# Revit family: equip-bottle-filler-elkay-LK4405FRK
name_source: partatom
category: Plumbing Fixtures
units: mm (PartAtom-declared; Revit-internal decimal feet)

## family parameters
Always vertical = Yes
Cut with Voids When Loaded = No
OmniClass Number = 23.45.00.00
OmniClass Title = Sanitary, Laundry, and Cleaning Equipment
Part Type = Normal
Room Calculation Point = No
Round Connector Dimension = Use Radius
Shared = No
Work Plane-Based = No

## types (1)
- LK4405FRK
    Activation = Push Button
    Apparent Load Phase 1 = 0 VA
    Body Material = Metal - Steel - Stainless - Chrome
    Bubbler = Vandal Resistant
    CW Connection = Yes
    Chiller Option = No
    Description = Bottle Filler
    Filter = Non-filtered
    Fountain = LK4405
    HW Connection = No
    Manufacturer = Elkay
    Model = LK4405FRK
    Mounting = Wall mount
    Number of Poles = 1
    Power Factor = 0
    Sanitary Service Size Radius = 0' - 0"
    Type = Outdoor
    URL = http://www.eklayusa.com
    Vent Connection = No
    Version = 1.0.0.0
    Voltage = 0 V
    Wall Plate Material = Metal - Steel - Stainless - Chrome
    Waste Connection = Yes
    Water Service Flow = 0 GPM
    Water Service Flow Out = 0 GPM
    Water Service Radius = 0' - 0"
    Water Service Size Radius = 0' - 0 3/16"

## geometry (parser evidence)
native form markers: Sweep x2
no freeform markers — native parametric forms only
